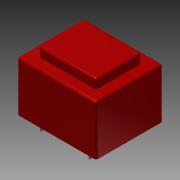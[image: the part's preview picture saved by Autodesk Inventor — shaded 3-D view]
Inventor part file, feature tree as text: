
AUTODESK INVENTOR PART (.ipt)
format: ipt  version: 2015 (Build 190159000, 159)  size: 241,152 bytes
history: native  units: mm
features: extrude x3, fillet x3, sketch x3
ambient origin geometry x8: Origin, YZ Plane, XZ Plane, XY Plane, X Axis, Y Axis, Z Axis, Center Point
bodies: Solid1 (feature_tree)
feature tree (9):
  extrude  "Extrusion1"  Depth=27.6mm
  extrude  "Extrusion2"  Depth=20.5mm
  extrude  "Extrusion3"  Depth=1.0mm
  fillet  "Fillet3"  Radius=20.0mm
  fillet  "Fillet4"  Radius=6.3mm
  fillet  "Fillet5"  Radius=5.0mm
  sketch  "Sketch1"  dims[d0=32.6mm d1=27.6mm]
  sketch  "Sketch2"  dims[d2=20.5mm d3=0.0mm d4=4.5mm]
  sketch  "Sketch3"  dims[d5=3.8mm d6=0.0mm d7=3.8mm d8=20.0mm d9=6.3mm d10=5.0mm d11=10.0mm d12=5.0mm d13=0.8mm d14=0.8mm d15=0.8mm d16=0.8mm d17=4.5mm d18=0.0mm d21=1.0mm d22=1.0mm d23=1.0mm]
